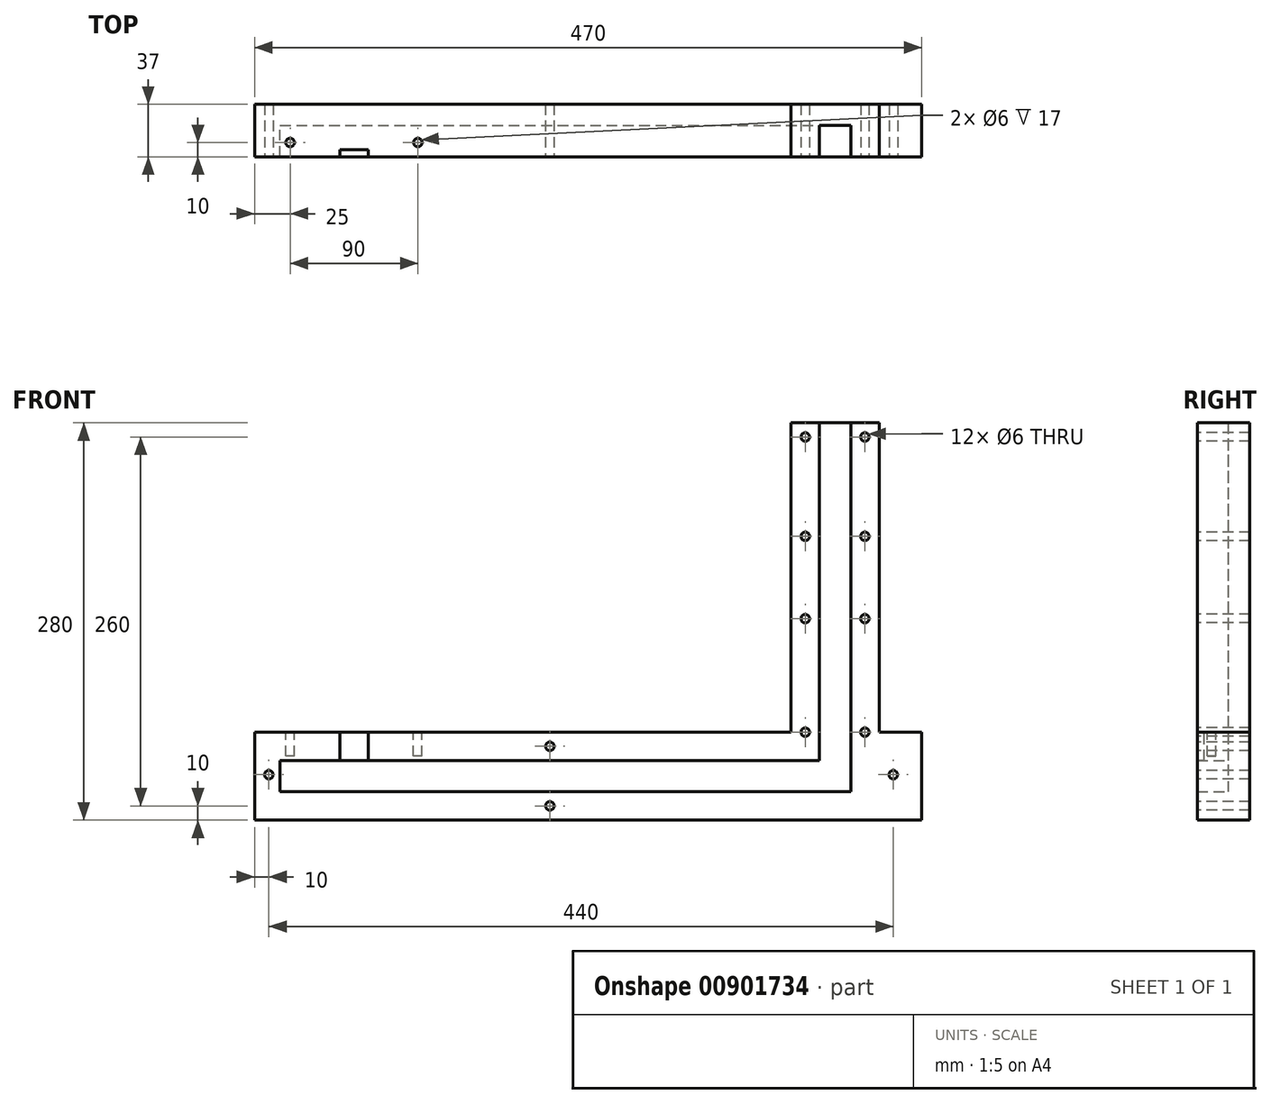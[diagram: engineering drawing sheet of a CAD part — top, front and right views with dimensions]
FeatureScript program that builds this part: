
annotation { "Feature Type Name" : "Feature", "Feature Type Description" : "" }
export const myFeature = defineFeature(function(context is Context, id is Id, definition is map)
    precondition{}
    {
        {
            var Q0;
            Q0=qCreatedBy(makeId("Front.planeOp"),FACE);
            var sketch = newSketch(context, id + "F0", { "sketchPlane" : qUnion([Q0])});
            skLineSegment(sketch, "E0", {"start": v(0, 0) * mm, "end": v(0, -280) * mm});
            skLineSegment(sketch, "E1", {"start": v(0, -280) * mm, "end": v(-440, -280) * mm});
            skLineSegment(sketch, "E2", {"start": v(-440, -218) * mm, "end": v(-62, -218) * mm});
            skLineSegment(sketch, "E3", {"start": v(-62, -218) * mm, "end": v(-62, 0) * mm});
            skLineSegment(sketch, "E4", {"start": v(-440, -218) * mm, "end": v(-440, -280) * mm});
            skLineSegment(sketch, "E5", {"start": v(-62, 0) * mm, "end": v(0, 0) * mm});
            skSolve(sketch);
        }
        {
            var Q0;
            Q0=makeQuery(id+"F0.imprint","IMPRINT",FACE,{"disambiguationData":[TD([[makeQuery(id+"F0.imprint","IMPRINT",EDGE,{"derivedFrom":sQuery(id+"F0.wireOp",EDGE,"E0")}),-1.0]])]});
            extrude(context, id + "F1", {"entities" : qUnion([Q0]), "depth" : 37 * mm, "offsetDistance" : 25 * mm});
        }
        {
            var Q0;
            Q0=makeQuery(id+"F1.opExtrude","SWEPT_FACE",FACE,{"disambiguationData":[OSD([sQuery(id+"F0.wireOp",EDGE,"E5")])]});
            var sketch = newSketch(context, id + "F2", { "sketchPlane" : qUnion([Q0])});
            skLineSegment(sketch, "E6.bottom", {"start": v(-42, -37) * mm, "end": v(-20, -37) * mm});
            skLineSegment(sketch, "E6.top", {"start": v(-42, -15) * mm, "end": v(-20, -15) * mm});
            skLineSegment(sketch, "E6.left", {"start": v(-42, -37) * mm, "end": v(-42, -15) * mm});
            skLineSegment(sketch, "E6.right", {"start": v(-20, -37) * mm, "end": v(-20, -15) * mm});
            skSolve(sketch);
        }
        {
            var Q0;
            Q0 = qSketchRegion(id + "F2", true);
            extrude(context, id + "F3", {"entities" : qUnion([Q0]), "operationType" : NewBodyOperationType.REMOVE, "oppositeDirection" : true, "depth" : 260 * mm, "offsetDistance" : 25 * mm});
        }
        {
            var Q0;
            Q0=makeQuery(id+"F1.opExtrude","SWEPT_FACE",FACE,{"disambiguationData":[OSD([sQuery(id+"F0.wireOp",EDGE,"E0")])]});
            var sketch = newSketch(context, id + "F4", { "sketchPlane" : qUnion([Q0])});
            skLineSegment(sketch, "E7.bottom", {"start": v(-37, -280) * mm, "end": v(0, -280) * mm});
            skLineSegment(sketch, "E7.top", {"start": v(-37, -218) * mm, "end": v(0, -218) * mm});
            skLineSegment(sketch, "E7.left", {"start": v(-37, -280) * mm, "end": v(-37, -218) * mm});
            skLineSegment(sketch, "E7.right", {"start": v(0, -280) * mm, "end": v(0, -218) * mm});
            skSolve(sketch);
        }
        {
            var Q0;
            Q0 = qSketchRegion(id + "F4", true);
            extrude(context, id + "F5", {"entities" : qUnion([Q0]), "operationType" : NewBodyOperationType.ADD, "depth" : 30 * mm, "offsetDistance" : 25 * mm});
        }
        {
            var Q0;
            Q0=makeQuery(id+"F3.boolean.opBoolean","COPY",FACE,{"derivedFrom":makeQuery(id+"F3.opExtrude","SWEPT_FACE",FACE,{"disambiguationData":[OSD([sQuery(id+"F2.wireOp",EDGE,"E6.left")])]})});
            var sketch = newSketch(context, id + "F6", { "sketchPlane" : qUnion([Q0])});
            skLineSegment(sketch, "E8.bottom", {"start": v(-37, -260) * mm, "end": v(-15, -260) * mm});
            skLineSegment(sketch, "E8.top", {"start": v(-37, -238) * mm, "end": v(-15, -238) * mm});
            skLineSegment(sketch, "E8.left", {"start": v(-37, -260) * mm, "end": v(-37, -238) * mm});
            skLineSegment(sketch, "E8.right", {"start": v(-15, -260) * mm, "end": v(-15, -238) * mm});
            skSolve(sketch);
        }
        {
            var Q0;
            Q0=makeQuery(id+"F6.imprint","IMPRINT",FACE,{"disambiguationData":[TD([[makeQuery(id+"F6.imprint","IMPRINT",EDGE,{"derivedFrom":sQuery(id+"F6.wireOp",EDGE,"E8.bottom")}),1.0]])]});
            extrude(context, id + "F7", {"entities" : qUnion([Q0]), "operationType" : NewBodyOperationType.REMOVE, "oppositeDirection" : true, "depth" : 380 * mm, "offsetDistance" : 25 * mm});
        }
        {
            var Q0;
            Q0=makeQuery(id+"F1.opExtrude","SWEPT_FACE",FACE,{"disambiguationData":[OSD([sQuery(id+"F0.wireOp",EDGE,"E2")])]});
            var sketch = newSketch(context, id + "F8", { "sketchPlane" : qUnion([Q0])});
            skLineSegment(sketch, "E9.bottom", {"start": v(-380, -37) * mm, "end": v(-360, -37) * mm});
            skLineSegment(sketch, "E9.top", {"start": v(-380, -32) * mm, "end": v(-360, -32) * mm});
            skLineSegment(sketch, "E9.left", {"start": v(-380, -37) * mm, "end": v(-380, -32) * mm});
            skLineSegment(sketch, "E9.right", {"start": v(-360, -37) * mm, "end": v(-360, -32) * mm});
            skSolve(sketch);
        }
        {
            var Q0;
            Q0=makeQuery(id+"F8.imprint","IMPRINT",FACE,{"disambiguationData":[TD([[makeQuery(id+"F8.imprint","IMPRINT",EDGE,{"derivedFrom":sQuery(id+"F8.wireOp",EDGE,"E9.bottom")}),1.0]])]});
            extrude(context, id + "F9", {"entities" : qUnion([Q0]), "operationType" : NewBodyOperationType.REMOVE, "oppositeDirection" : true, "depth" : 25 * mm, "offsetDistance" : 25 * mm});
        }
        {
            var Q0;
            {var subQ0=sQuery(id+"F0.wireOp",EDGE,"E5");var subQ1=sQuery(id+"F0.wireOp",EDGE,"E3");var subQ2=sQuery(id+"F0.wireOp",EDGE,"E2");Q0=makeQuery(id+"F9.boolean.opBoolean","SPLIT",FACE,{"disambiguationData":[TD([makeQuery(id+"F1.opExtrude","SWEPT_FACE",FACE,{"disambiguationData":[OSD([subQ1])]})])],"derivedFrom":makeQuery(id+"F5.boolean.opBoolean","MERGE",FACE,{"derivedFrom":[makeQuery(id+"F1.opExtrude","CAP_FACE",FACE,{"disambiguationData":[OSD([sQuery(id+"F0.wireOp",EDGE,"E0"),sQuery(id+"F0.wireOp",EDGE,"E1"),subQ2,subQ1,sQuery(id+"F0.wireOp",EDGE,"E4"),subQ0])],"isStart":false}),makeQuery(id+"F5.opExtrude","SWEPT_FACE",FACE,{"disambiguationData":[OSD([sQuery(id+"F4.wireOp",EDGE,"E7.left")])]})]})});}
            var sketch = newSketch(context, id + "F10", { "sketchPlane" : qUnion([Q0])});
            skCircle(sketch, "E10", {"center": v(-52, -10) * mm, "radius": 3 * mm});
            skCircle(sketch, "E11", {"center": v(-10, -10) * mm, "radius": 3 * mm});
            skCircle(sketch, "E12", {"center": v(-52, -80) * mm, "radius": 3 * mm});
            skCircle(sketch, "E13", {"center": v(-10, -80) * mm, "radius": 3 * mm});
            skCircle(sketch, "E14", {"center": v(-52, -138) * mm, "radius": 3 * mm});
            skCircle(sketch, "E15", {"center": v(-10, -138) * mm, "radius": 3 * mm});
            skCircle(sketch, "E16", {"center": v(-52, -218) * mm, "radius": 3 * mm});
            skCircle(sketch, "E17", {"center": v(-10, -218) * mm, "radius": 3 * mm});
            skCircle(sketch, "E18", {"center": v(10, -248) * mm, "radius": 3 * mm});
            skCircle(sketch, "E19", {"center": v(-232, -270) * mm, "radius": 3 * mm});
            skCircle(sketch, "E20", {"center": v(-232, -228) * mm, "radius": 3 * mm});
            skCircle(sketch, "E21", {"center": v(-430, -248) * mm, "radius": 3 * mm});
            skSolve(sketch);
        }
        {
            var Q0;
            Q0 = qSketchRegion(id + "F10", true);
            extrude(context, id + "F11", {"entities" : qUnion([Q0]), "operationType" : NewBodyOperationType.REMOVE, "endBound" : BoundingType.THROUGH_ALL, "oppositeDirection" : true, "depth" : 25 * mm, "offsetDistance" : 25 * mm});
        }
        {
            var Q0;
            Q0=makeQuery(id+"F1.opExtrude","SWEPT_FACE",FACE,{"disambiguationData":[OSD([sQuery(id+"F0.wireOp",EDGE,"E2")])]});
            var sketch = newSketch(context, id + "F12", { "sketchPlane" : qUnion([Q0])});
            skSolve(sketch);
        }
        {
            var Q0;
            {var subQ0=sQuery(id+"F0.wireOp",EDGE,"E2");Q0=makeQuery(id+"F12.imprint","IMPRINT",FACE,{"disambiguationData":[TD([[makeQuery(id+"F12.imprint","IMPRINT",EDGE,{"derivedFrom":makeQuery(id+"F1.opExtrude","CAP_EDGE",EDGE,{"disambiguationData":[OSD([subQ0])],"isStart":true})}),-1.0]])]});}
            var sketch = newSketch(context, id + "F13", { "sketchPlane" : qUnion([Q0])});
            skCircle(sketch, "E22", {"center": v(-415, -27) * mm, "radius": 3 * mm});
            skCircle(sketch, "E23", {"center": v(-325, -27) * mm, "radius": 3 * mm});
            skSolve(sketch);
        }
        {
            var Q0;
            Q0 = qSketchRegion(id + "F13", true);
            extrude(context, id + "F14", {"entities" : qUnion([Q0]), "operationType" : NewBodyOperationType.REMOVE, "oppositeDirection" : true, "depth" : 17 * mm, "offsetDistance" : 25 * mm});
        }
    });
